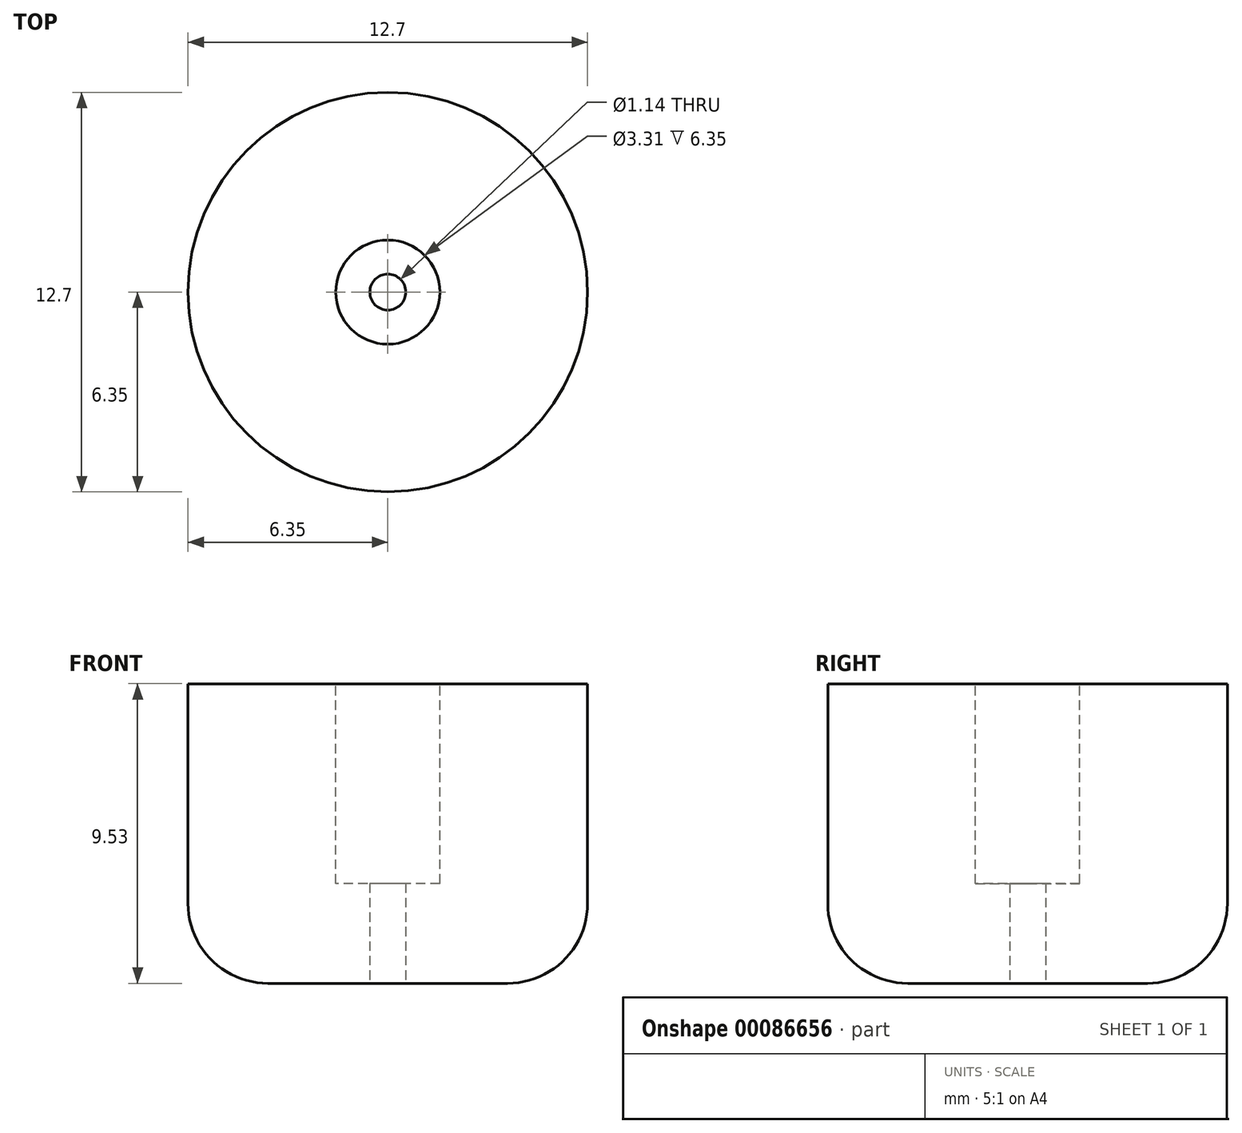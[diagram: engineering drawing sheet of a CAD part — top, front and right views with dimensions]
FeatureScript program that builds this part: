
annotation { "Feature Type Name" : "Feature", "Feature Type Description" : "" }
export const myFeature = defineFeature(function(context is Context, id is Id, definition is map)
    precondition{}
    {
        {
            var Q0;
            Q0=qCreatedBy(makeId("Top.planeOp"),FACE);
            var sketch = newSketch(context, id + "F0", { "sketchPlane" : qUnion([Q0])});
            skCircle(sketch, "E0", {"center": v(0, 0) * mm, "radius": 6.35 * mm});
            skCircle(sketch, "E1", {"center": v(0, 0) * mm, "radius": 0.57 * mm});
            skSolve(sketch);
        }
        {
            var Q0;
            Q0=makeQuery(id+"F0.imprint","IMPRINT",FACE,{"disambiguationData":[TD([[makeQuery(id+"F0.imprint","IMPRINT",EDGE,{"derivedFrom":sQuery(id+"F0.wireOp",EDGE,"E0")}),1.0]])]});
            extrude(context, id + "F1", {"entities" : qUnion([Q0]), "depth" : 9.52 * mm});
        }
        {
            var Q0;
            Q0=makeQuery(id+"F1.opExtrude","CAP_FACE",FACE,{"disambiguationData":[OSD([sQuery(id+"F0.wireOp",EDGE,"E0"),sQuery(id+"F0.wireOp",EDGE,"E1")])],"isStart":false});
            var sketch = newSketch(context, id + "F2", { "sketchPlane" : qUnion([Q0])});
            skCircle(sketch, "E2", {"center": v(0, 0) * mm, "radius": 1.66 * mm});
            skSolve(sketch);
        }
        {
            var Q0;
            Q0=makeQuery(id+"F2.imprint","IMPRINT",FACE,{"disambiguationData":[TD([[makeQuery(id+"F2.imprint","IMPRINT",EDGE,{"derivedFrom":sQuery(id+"F2.wireOp",EDGE,"E2")}),1.0]])]});
            extrude(context, id + "F3", {"entities" : qUnion([Q0]), "operationType" : NewBodyOperationType.REMOVE, "oppositeDirection" : true, "depth" : 6.35 * mm});
        }
        {
            var Q0;
            Q0=makeQuery(id+"F1.opExtrude","CAP_EDGE",EDGE,{"disambiguationData":[OSD([sQuery(id+"F0.wireOp",EDGE,"E0")])],"isStart":true});
            fillet(context, id + "F4", {"entities" : qUnion([Q0]), "radius" : 2.54 * mm, "tangentPropagation" : true, "allowEdgeOverflow" : false});
        }
    });
